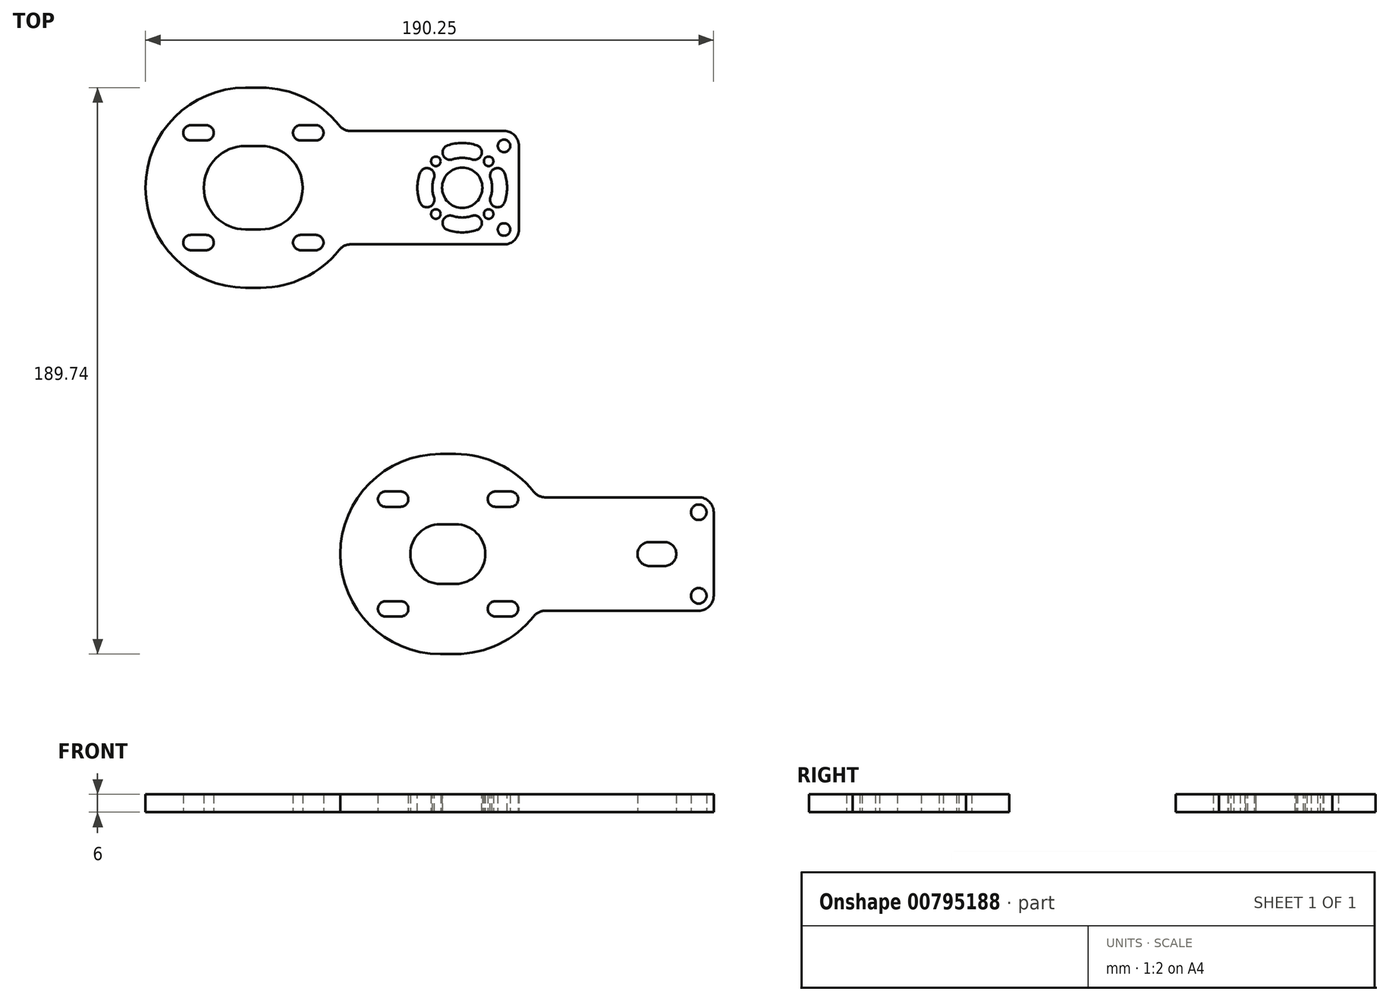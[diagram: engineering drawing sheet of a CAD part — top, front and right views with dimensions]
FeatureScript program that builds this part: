
annotation { "Feature Type Name" : "Feature", "Feature Type Description" : "" }
export const myFeature = defineFeature(function(context is Context, id is Id, definition is map)
    precondition{}
    {
        {
            var Q0;
            Q0=qCreatedBy(makeId("Top.planeOp"),FACE);
            var sketch = newSketch(context, id + "F0", { "sketchPlane" : qUnion([Q0])});
            skLineSegment(sketch, "E0.left", {"start": v(0, 33.5) * mm, "end": v(-0.07, -16.5) * mm, "construction": true});
            skLineSegment(sketch, "E0.right", {"start": v(90, 33.37) * mm, "end": v(89.93, -16.63) * mm});
            skCircle(sketch, "E1", {"center": v(69.95, 0) * mm, "radius": 6.75 * mm, "construction": true});
            skLineSegment(sketch, "E2.bottom", {"start": v(45.4, -41.12) * mm, "end": v(-45.4, -41.12) * mm, "construction": true});
            skLineSegment(sketch, "E2.top", {"start": v(45.4, 41.12) * mm, "end": v(-45.4, 41.12) * mm, "construction": true});
            skLineSegment(sketch, "E2.right", {"start": v(-45.4, -41.12) * mm, "end": v(-45.4, 41.12) * mm, "construction": true});
            skPoint(sketch, "E2.middle", {"position": v(0, 0) * mm});
            skCircle(sketch, "E3", {"center": v(69.95, 0) * mm, "radius": 6.75 * mm});
            skLineSegment(sketch, "E4", {"start": v(69.95, 0) * mm, "end": v(61.11, 8.84) * mm, "construction": true});
            skCircle(sketch, "E5", {"center": v(61.11, 8.84) * mm, "radius": 1.6 * mm});
            skCircle(sketch, "E6.1.0", {"center": v(61.11, -8.84) * mm, "radius": 1.6 * mm});
            skCircle(sketch, "E6.2.0", {"center": v(78.8, -8.84) * mm, "radius": 1.6 * mm});
            skCircle(sketch, "E6.3.0", {"center": v(78.8, 8.84) * mm, "radius": 1.6 * mm});
            skLineSegment(sketch, "E7", {"start": v(61.11, 8.84) * mm, "end": v(66.11, 8.84) * mm});
            skLineSegment(sketch, "E8", {"start": v(61.11, -8.84) * mm, "end": v(66.11, -8.84) * mm});
            skLineSegment(sketch, "E9", {"start": v(78.8, -8.84) * mm, "end": v(83.8, -8.84) * mm});
            skLineSegment(sketch, "E10", {"start": v(78.8, 8.84) * mm, "end": v(83.8, 8.84) * mm});
            skLineSegment(sketch, "E11", {"start": v(69.95, 0) * mm, "end": v(74.95, 0) * mm});
            skArc(sketch, "E12.0.startCap", {"start": v(78.8, 7.24) * mm, "mid": v(77.2, 8.84) * mm, "end": v(78.8, 10.44) * mm});
            skArc(sketch, "E12.0.endCap", {"start": v(83.8, 10.44) * mm, "mid": v(85.4, 8.84) * mm, "end": v(83.8, 7.24) * mm});
            skArc(sketch, "E13.0.startCap", {"start": v(61.11, 7.24) * mm, "mid": v(59.51, 8.84) * mm, "end": v(61.11, 10.44) * mm});
            skArc(sketch, "E13.1.startCap", {"start": v(61.11, -10.44) * mm, "mid": v(59.51, -8.84) * mm, "end": v(61.11, -7.24) * mm});
            skArc(sketch, "E13.2.startCap", {"start": v(78.8, -10.44) * mm, "mid": v(77.2, -8.84) * mm, "end": v(78.8, -7.24) * mm});
            skArc(sketch, "E13.2.endCap", {"start": v(83.8, -7.24) * mm, "mid": v(85.4, -8.84) * mm, "end": v(83.8, -10.44) * mm});
            skArc(sketch, "E14.0.startCap", {"start": v(69.95, -6.75) * mm, "mid": v(63.2, 0) * mm, "end": v(69.95, 6.75) * mm});
            skArc(sketch, "E14.0.endCap", {"start": v(74.95, 6.75) * mm, "mid": v(81.7, 0) * mm, "end": v(74.95, -6.75) * mm});
            skArc(sketch, "E15", {"start": v(74.95, -19) * mm, "mid": v(93.95, 0) * mm, "end": v(74.95, 19) * mm, "construction": true});
            skLineSegment(sketch, "E16", {"start": v(74.95, 19) * mm, "end": v(32.6, 19) * mm});
            skLineSegment(sketch, "E17", {"start": v(74.95, -19) * mm, "end": v(32.6, -19) * mm});
            skPoint(sketch, "E18.visualSharp", {"position": v(27.6, 19) * mm});
            skCircle(sketch, "E19", {"center": v(0, 0) * mm, "radius": 26 * mm, "construction": true});
            skCircle(sketch, "E20", {"center": v(0, 0) * mm, "radius": 16 * mm, "construction": true});
            skLineSegment(sketch, "E21", {"start": v(0, 0) * mm, "end": v(-28.53, 28.53) * mm, "construction": true});
            skCircle(sketch, "E22", {"center": v(-18.38, 18.38) * mm, "radius": 2.55 * mm, "construction": true});
            skCircle(sketch, "E23.1.0", {"center": v(-18.38, -18.38) * mm, "radius": 2.55 * mm, "construction": true});
            skCircle(sketch, "E23.2.0", {"center": v(18.38, -18.38) * mm, "radius": 2.55 * mm, "construction": true});
            skCircle(sketch, "E23.3.0", {"center": v(18.38, 18.38) * mm, "radius": 2.55 * mm, "construction": true});
            skLineSegment(sketch, "E24", {"start": v(15.83, 18.38) * mm, "end": v(20.93, 18.38) * mm});
            skLineSegment(sketch, "E25", {"start": v(15.83, -18.38) * mm, "end": v(20.93, -18.38) * mm});
            skLineSegment(sketch, "E26", {"start": v(-20.93, -18.38) * mm, "end": v(-15.83, -18.38) * mm});
            skLineSegment(sketch, "E27", {"start": v(-20.93, 18.38) * mm, "end": v(-15.83, 18.38) * mm});
            skArc(sketch, "E28.0.startCap", {"start": v(-20.93, 15.83) * mm, "mid": v(-23.48, 18.38) * mm, "end": v(-20.93, 20.93) * mm});
            skArc(sketch, "E28.0.endCap", {"start": v(-15.83, 20.93) * mm, "mid": v(-13.28, 18.38) * mm, "end": v(-15.83, 15.83) * mm});
            skLineSegment(sketch, "E28.0.left", {"start": v(-20.93, 20.93) * mm, "end": v(-15.83, 20.93) * mm});
            skLineSegment(sketch, "E28.0.right", {"start": v(-20.93, 15.83) * mm, "end": v(-15.83, 15.83) * mm});
            skArc(sketch, "E29.0.startCap", {"start": v(15.83, 15.83) * mm, "mid": v(13.28, 18.38) * mm, "end": v(15.83, 20.93) * mm});
            skArc(sketch, "E29.0.endCap", {"start": v(20.93, 20.93) * mm, "mid": v(23.48, 18.38) * mm, "end": v(20.93, 15.83) * mm});
            skLineSegment(sketch, "E29.0.left", {"start": v(15.83, 20.93) * mm, "end": v(20.93, 20.93) * mm});
            skLineSegment(sketch, "E29.0.right", {"start": v(15.83, 15.83) * mm, "end": v(20.93, 15.83) * mm});
            skArc(sketch, "E30.0.startCap", {"start": v(15.83, -20.93) * mm, "mid": v(13.28, -18.38) * mm, "end": v(15.83, -15.83) * mm});
            skArc(sketch, "E30.0.endCap", {"start": v(20.93, -15.83) * mm, "mid": v(23.48, -18.38) * mm, "end": v(20.93, -20.93) * mm});
            skLineSegment(sketch, "E30.0.left", {"start": v(15.83, -15.83) * mm, "end": v(20.93, -15.83) * mm});
            skLineSegment(sketch, "E30.0.right", {"start": v(15.83, -20.93) * mm, "end": v(20.93, -20.93) * mm});
            skArc(sketch, "E31.0.startCap", {"start": v(-20.93, -20.93) * mm, "mid": v(-23.48, -18.38) * mm, "end": v(-20.93, -15.83) * mm});
            skArc(sketch, "E31.0.endCap", {"start": v(-15.83, -15.83) * mm, "mid": v(-13.28, -18.38) * mm, "end": v(-15.83, -20.93) * mm});
            skLineSegment(sketch, "E31.0.left", {"start": v(-20.93, -15.83) * mm, "end": v(-15.83, -15.83) * mm});
            skLineSegment(sketch, "E31.0.right", {"start": v(-20.93, -20.93) * mm, "end": v(-15.83, -20.93) * mm});
            skLineSegment(sketch, "E32", {"start": v(2.5, 0) * mm, "end": v(-2.6, 0) * mm});
            skArc(sketch, "E33.0.startCap", {"start": v(2.5, 14) * mm, "mid": v(16.5, 0) * mm, "end": v(2.5, -14) * mm});
            skArc(sketch, "E33.0.endCap", {"start": v(-2.6, -14) * mm, "mid": v(-16.6, 0) * mm, "end": v(-2.6, 14) * mm});
            skLineSegment(sketch, "E33.0.left", {"start": v(2.5, -14) * mm, "end": v(-2.6, -14) * mm});
            skLineSegment(sketch, "E33.0.right", {"start": v(2.5, 14) * mm, "end": v(-2.6, 14) * mm});
            skArc(sketch, "E34.0.startCap", {"start": v(2.5, 33.5) * mm, "mid": v(17.04, 30.18) * mm, "end": v(28.7, 20.88) * mm});
            skArc(sketch, "E34.0.endCap", {"start": v(-2.6, -33.5) * mm, "mid": v(-36.1, 0) * mm, "end": v(-2.6, 33.5) * mm});
            skLineSegment(sketch, "E34.0.left", {"start": v(2.5, -33.5) * mm, "end": v(-2.6, -33.5) * mm});
            skLineSegment(sketch, "E34.0.right", {"start": v(2.5, 33.5) * mm, "end": v(-2.6, 33.5) * mm});
            skArc(sketch, "E35.trimOffspring", {"start": v(28.7, -20.88) * mm, "mid": v(17.04, -30.18) * mm, "end": v(2.5, -33.5) * mm});
            skPoint(sketch, "E36.visualSharp", {"position": v(30.1, 19) * mm});
            skArc(sketch, "E36.filletArc", {"start": v(28.7, 20.88) * mm, "mid": v(30.44, 19.5) * mm, "end": v(32.6, 19) * mm});
            skPoint(sketch, "E37.visualSharp", {"position": v(30.1, -19) * mm});
            skArc(sketch, "E37.filletArc", {"start": v(32.6, -19) * mm, "mid": v(30.44, -19.5) * mm, "end": v(28.7, -20.88) * mm});
            skLineSegment(sketch, "E38.bottom", {"start": v(83.95, 19) * mm, "end": v(50.95, 19) * mm});
            skLineSegment(sketch, "E38.top", {"start": v(83.95, -19) * mm, "end": v(50.95, -19) * mm});
            skLineSegment(sketch, "E38.left", {"start": v(88.95, 14) * mm, "end": v(88.95, -14) * mm});
            skLineSegment(sketch, "E38.right", {"start": v(50.95, 19) * mm, "end": v(50.95, -19) * mm});
            skPoint(sketch, "E39.visualSharp", {"position": v(88.95, 19) * mm});
            skArc(sketch, "E39.filletArc", {"start": v(88.95, 14) * mm, "mid": v(87.49, 17.54) * mm, "end": v(83.95, 19) * mm});
            skPoint(sketch, "E40.visualSharp", {"position": v(88.95, -19) * mm});
            skArc(sketch, "E40.filletArc", {"start": v(83.95, -19) * mm, "mid": v(87.49, -17.54) * mm, "end": v(88.95, -14) * mm});
            skCircle(sketch, "E41", {"center": v(83.95, 14) * mm, "radius": 2.1 * mm});
            skCircle(sketch, "E42", {"center": v(83.95, -14) * mm, "radius": 2.1 * mm});
            skSolve(sketch);
        }
        {
            var Q0;
            Q0=qSketchRegion(id+"F0",true);
            extrude(context, id + "F1", {"entities" : qUnion([Q0]), "depth" : 6 * mm, "offsetDistance" : 25 * mm});
        }
        {
            var Q0;
            Q0=makeQuery(id+"F1.opExtrude","CAP_FACE",FACE,{"disambiguationData":[OSD([sQuery(id+"F0.wireOp",EDGE,"H2Rf1mUt-0jlt-27wB-YffO-BGlGPGkjmCcf"),sQuery(id+"F0.wireOp",EDGE,"pAdha1hi-vLvk-yrs3-a5r3-yK9QRZCf7Ppp"),sQuery(id+"F0.wireOp",EDGE,"qyuHHp5k-pOz1-b6pl-9DLs-GjlQiXBvs5dg"),sQuery(id+"F0.wireOp",EDGE,"E3"),sQuery(id+"F0.wireOp",EDGE,"E5"),sQuery(id+"F0.wireOp",EDGE,"E6.1.0"),sQuery(id+"F0.wireOp",EDGE,"E6.2.0"),sQuery(id+"F0.wireOp",EDGE,"E6.3.0"),sQuery(id+"F0.wireOp",EDGE,"E16"),sQuery(id+"F0.wireOp",EDGE,"E17"),sQuery(id+"F0.wireOp",EDGE,"E18.filletArc"),sQuery(id+"F0.wireOp",EDGE,"bb5d5ffc-c1ad-4c8e-af76-ad25ce88a9b4.filletArc"),sQuery(id+"F0.wireOp",EDGE,"E22"),sQuery(id+"F0.wireOp",EDGE,"E23.1.0"),sQuery(id+"F0.wireOp",EDGE,"E23.2.0"),sQuery(id+"F0.wireOp",EDGE,"E23.3.0")])],"isStart":false});
            var sketch = newSketch(context, id + "F2", { "sketchPlane" : qUnion([Q0])});
            skArc(sketch, "E43", {"start": v(58.13, 4.07) * mm, "mid": v(57.45, 0) * mm, "end": v(58.13, -4.07) * mm});
            skLineSegment(sketch, "E44", {"start": v(69.95, 0) * mm, "end": v(55.62, 4.93) * mm, "construction": true});
            skLineSegment(sketch, "E45", {"start": v(69.95, 0) * mm, "end": v(55.25, -5.06) * mm, "construction": true});
            skArc(sketch, "E46.0.startCap", {"start": v(55.77, 4.88) * mm, "mid": v(58.95, 6.43) * mm, "end": v(60.5, 3.26) * mm});
            skArc(sketch, "E46.0.endCap", {"start": v(60.5, -3.26) * mm, "mid": v(58.95, -6.43) * mm, "end": v(55.77, -4.88) * mm});
            skArc(sketch, "E46.0.left", {"start": v(60.5, 3.26) * mm, "mid": v(59.95, 0) * mm, "end": v(60.5, -3.26) * mm});
            skArc(sketch, "E46.0.right", {"start": v(55.77, 4.88) * mm, "mid": v(54.95, 0) * mm, "end": v(55.77, -4.88) * mm});
            skArc(sketch, "E47.1.0", {"start": v(65.07, -14.18) * mm, "mid": v(63.52, -11) * mm, "end": v(66.7, -9.46) * mm});
            skArc(sketch, "E47.1.1", {"start": v(66.7, -9.46) * mm, "mid": v(69.95, -10) * mm, "end": v(73.2, -9.46) * mm});
            skArc(sketch, "E47.1.2", {"start": v(73.2, -9.46) * mm, "mid": v(76.39, -11) * mm, "end": v(74.84, -14.18) * mm});
            skArc(sketch, "E47.1.3", {"start": v(65.07, -14.18) * mm, "mid": v(69.95, -15) * mm, "end": v(74.84, -14.18) * mm});
            skArc(sketch, "E47.2.0", {"start": v(84.14, -4.88) * mm, "mid": v(80.96, -6.43) * mm, "end": v(79.4, -3.26) * mm});
            skArc(sketch, "E47.2.1", {"start": v(79.4, -3.26) * mm, "mid": v(79.95, 0) * mm, "end": v(79.4, 3.26) * mm});
            skArc(sketch, "E47.2.2", {"start": v(79.4, 3.26) * mm, "mid": v(80.96, 6.43) * mm, "end": v(84.14, 4.88) * mm});
            skArc(sketch, "E47.2.3", {"start": v(84.14, -4.88) * mm, "mid": v(84.95, 0) * mm, "end": v(84.14, 4.88) * mm});
            skArc(sketch, "E47.3.0", {"start": v(74.84, 14.18) * mm, "mid": v(76.39, 11) * mm, "end": v(73.2, 9.46) * mm});
            skArc(sketch, "E47.3.1", {"start": v(73.2, 9.46) * mm, "mid": v(69.95, 10) * mm, "end": v(66.7, 9.46) * mm});
            skArc(sketch, "E47.3.2", {"start": v(66.7, 9.46) * mm, "mid": v(63.52, 11) * mm, "end": v(65.07, 14.18) * mm});
            skArc(sketch, "E47.3.3", {"start": v(74.84, 14.18) * mm, "mid": v(69.95, 15) * mm, "end": v(65.07, 14.18) * mm});
            skSolve(sketch);
        }
        {
            var Q0;
            Q0=qSketchRegion(id+"F2",true);
            extrude(context, id + "F3", {"entities" : qUnion([Q0]), "operationType" : NewBodyOperationType.REMOVE, "oppositeDirection" : true, "depth" : 25 * mm, "offsetDistance" : 25 * mm});
        }
        {
            var Q0;
            Q0=qCreatedBy(makeId("Top.planeOp"),FACE);
            var sketch = newSketch(context, id + "F4", { "sketchPlane" : qUnion([Q0])});
            skLineSegment(sketch, "E48.left", {"start": v(65.2, -89.24) * mm, "end": v(65.13, -139.24) * mm, "construction": true});
            skPoint(sketch, "E49.middle", {"position": v(65.2, -122.74) * mm});
            skArc(sketch, "E50", {"start": v(140.15, -141.74) * mm, "mid": v(159.15, -122.74) * mm, "end": v(140.15, -103.74) * mm, "construction": true});
            skLineSegment(sketch, "E51", {"start": v(140.15, -103.74) * mm, "end": v(97.8, -103.74) * mm});
            skLineSegment(sketch, "E52", {"start": v(140.15, -141.74) * mm, "end": v(97.8, -141.74) * mm});
            skPoint(sketch, "E53.visualSharp", {"position": v(92.79, -103.74) * mm});
            skCircle(sketch, "E54", {"center": v(65.2, -122.74) * mm, "radius": 26 * mm, "construction": true});
            skCircle(sketch, "E55", {"center": v(65.2, -122.74) * mm, "radius": 16 * mm, "construction": true});
            skLineSegment(sketch, "E56", {"start": v(65.2, -122.74) * mm, "end": v(36.67, -94.2) * mm, "construction": true});
            skCircle(sketch, "E57", {"center": v(46.81, -104.35) * mm, "radius": 2.55 * mm, "construction": true});
            skCircle(sketch, "E58.1.0", {"center": v(46.81, -141.12) * mm, "radius": 2.55 * mm, "construction": true});
            skCircle(sketch, "E58.2.0", {"center": v(83.58, -141.12) * mm, "radius": 2.55 * mm, "construction": true});
            skCircle(sketch, "E58.3.0", {"center": v(83.58, -104.35) * mm, "radius": 2.55 * mm, "construction": true});
            skLineSegment(sketch, "E59", {"start": v(81.03, -104.35) * mm, "end": v(86.13, -104.35) * mm});
            skLineSegment(sketch, "E60", {"start": v(81.03, -141.12) * mm, "end": v(86.13, -141.12) * mm});
            skLineSegment(sketch, "E61", {"start": v(44.26, -141.12) * mm, "end": v(49.36, -141.12) * mm});
            skLineSegment(sketch, "E62", {"start": v(44.26, -104.35) * mm, "end": v(49.36, -104.35) * mm});
            skArc(sketch, "E63.0.startCap", {"start": v(44.26, -106.9) * mm, "mid": v(41.71, -104.35) * mm, "end": v(44.26, -101.8) * mm});
            skArc(sketch, "E63.0.endCap", {"start": v(49.36, -101.8) * mm, "mid": v(51.91, -104.35) * mm, "end": v(49.36, -106.9) * mm});
            skLineSegment(sketch, "E63.0.left", {"start": v(44.26, -101.8) * mm, "end": v(49.36, -101.8) * mm});
            skLineSegment(sketch, "E63.0.right", {"start": v(44.26, -106.9) * mm, "end": v(49.36, -106.9) * mm});
            skArc(sketch, "E64.0.startCap", {"start": v(81.03, -106.9) * mm, "mid": v(78.48, -104.35) * mm, "end": v(81.03, -101.8) * mm});
            skArc(sketch, "E64.0.endCap", {"start": v(86.13, -101.8) * mm, "mid": v(88.68, -104.35) * mm, "end": v(86.13, -106.9) * mm});
            skLineSegment(sketch, "E64.0.left", {"start": v(81.03, -101.8) * mm, "end": v(86.13, -101.8) * mm});
            skLineSegment(sketch, "E64.0.right", {"start": v(81.03, -106.9) * mm, "end": v(86.13, -106.9) * mm});
            skArc(sketch, "E65.0.startCap", {"start": v(81.03, -143.67) * mm, "mid": v(78.48, -141.12) * mm, "end": v(81.03, -138.57) * mm});
            skArc(sketch, "E65.0.endCap", {"start": v(86.13, -138.57) * mm, "mid": v(88.68, -141.12) * mm, "end": v(86.13, -143.67) * mm});
            skLineSegment(sketch, "E65.0.left", {"start": v(81.03, -138.57) * mm, "end": v(86.13, -138.57) * mm});
            skLineSegment(sketch, "E65.0.right", {"start": v(81.03, -143.67) * mm, "end": v(86.13, -143.67) * mm});
            skArc(sketch, "E66.0.startCap", {"start": v(44.26, -143.67) * mm, "mid": v(41.71, -141.12) * mm, "end": v(44.26, -138.57) * mm});
            skArc(sketch, "E66.0.endCap", {"start": v(49.36, -138.57) * mm, "mid": v(51.91, -141.12) * mm, "end": v(49.36, -143.67) * mm});
            skLineSegment(sketch, "E66.0.left", {"start": v(44.26, -138.57) * mm, "end": v(49.36, -138.57) * mm});
            skLineSegment(sketch, "E66.0.right", {"start": v(44.26, -143.67) * mm, "end": v(49.36, -143.67) * mm});
            skLineSegment(sketch, "E67", {"start": v(67.7, -122.74) * mm, "end": v(62.6, -122.74) * mm});
            skArc(sketch, "E68.0.startCap", {"start": v(67.7, -112.74) * mm, "mid": v(77.7, -122.74) * mm, "end": v(67.7, -132.74) * mm});
            skArc(sketch, "E68.0.endCap", {"start": v(62.6, -132.74) * mm, "mid": v(52.6, -122.74) * mm, "end": v(62.6, -112.74) * mm});
            skLineSegment(sketch, "E68.0.left", {"start": v(67.7, -132.74) * mm, "end": v(62.6, -132.74) * mm});
            skLineSegment(sketch, "E68.0.right", {"start": v(67.7, -112.74) * mm, "end": v(62.6, -112.74) * mm});
            skArc(sketch, "E69.0.startCap", {"start": v(67.7, -89.24) * mm, "mid": v(82.24, -92.56) * mm, "end": v(93.9, -101.85) * mm});
            skArc(sketch, "E69.0.endCap", {"start": v(62.6, -156.24) * mm, "mid": v(29.1, -122.74) * mm, "end": v(62.6, -89.24) * mm});
            skLineSegment(sketch, "E69.0.left", {"start": v(67.7, -156.24) * mm, "end": v(62.6, -156.24) * mm});
            skLineSegment(sketch, "E69.0.right", {"start": v(67.7, -89.24) * mm, "end": v(62.6, -89.24) * mm});
            skArc(sketch, "E70.trimOffspring", {"start": v(93.9, -143.62) * mm, "mid": v(82.24, -152.92) * mm, "end": v(67.7, -156.24) * mm});
            skPoint(sketch, "E71.visualSharp", {"position": v(95.3, -103.74) * mm});
            skArc(sketch, "E71.filletArc", {"start": v(93.9, -101.85) * mm, "mid": v(95.64, -103.24) * mm, "end": v(97.8, -103.74) * mm});
            skPoint(sketch, "E72.visualSharp", {"position": v(95.3, -141.74) * mm});
            skArc(sketch, "E72.filletArc", {"start": v(97.8, -141.74) * mm, "mid": v(95.64, -142.23) * mm, "end": v(93.9, -143.62) * mm});
            skLineSegment(sketch, "E73.bottom", {"start": v(149.15, -103.74) * mm, "end": v(116.15, -103.74) * mm});
            skLineSegment(sketch, "E73.top", {"start": v(149.15, -141.74) * mm, "end": v(116.15, -141.74) * mm});
            skLineSegment(sketch, "E73.left", {"start": v(154.15, -108.74) * mm, "end": v(154.15, -136.74) * mm});
            skPoint(sketch, "E74.visualSharp", {"position": v(154.15, -103.74) * mm});
            skArc(sketch, "E74.filletArc", {"start": v(154.15, -108.74) * mm, "mid": v(152.69, -105.2) * mm, "end": v(149.15, -103.74) * mm});
            skPoint(sketch, "E75.visualSharp", {"position": v(154.15, -141.74) * mm});
            skArc(sketch, "E75.filletArc", {"start": v(149.15, -141.74) * mm, "mid": v(152.69, -140.27) * mm, "end": v(154.15, -136.74) * mm});
            skLineSegment(sketch, "E76", {"start": v(135.15, -122.74) * mm, "end": v(126.31, -113.9) * mm, "construction": true});
            skPoint(sketch, "E77.center", {"position": v(135.15, -122.74) * mm});
            skLineSegment(sketch, "E78", {"start": v(126.31, -113.9) * mm, "end": v(131.31, -113.9) * mm});
            skLineSegment(sketch, "E79", {"start": v(126.31, -131.58) * mm, "end": v(131.31, -131.58) * mm});
            skLineSegment(sketch, "E80", {"start": v(144, -131.58) * mm, "end": v(149, -131.58) * mm});
            skLineSegment(sketch, "E81", {"start": v(144, -113.9) * mm, "end": v(149, -113.9) * mm});
            skArc(sketch, "E82.0.startCap", {"start": v(144, -115.5) * mm, "mid": v(142.4, -113.9) * mm, "end": v(144, -112.3) * mm});
            skArc(sketch, "E82.0.endCap", {"start": v(149, -112.3) * mm, "mid": v(150.6, -113.9) * mm, "end": v(149, -115.5) * mm});
            skArc(sketch, "E83.0.startCap", {"start": v(126.31, -115.5) * mm, "mid": v(124.71, -113.9) * mm, "end": v(126.31, -112.3) * mm});
            skArc(sketch, "E83.1.startCap", {"start": v(126.31, -133.18) * mm, "mid": v(124.71, -131.58) * mm, "end": v(126.31, -129.98) * mm});
            skArc(sketch, "E83.2.startCap", {"start": v(144, -133.18) * mm, "mid": v(142.4, -131.58) * mm, "end": v(144, -129.98) * mm});
            skArc(sketch, "E83.2.endCap", {"start": v(149, -129.98) * mm, "mid": v(150.6, -131.58) * mm, "end": v(149, -133.18) * mm});
            skArc(sketch, "E84.0.startCap", {"start": v(135.15, -129.49) * mm, "mid": v(128.4, -122.74) * mm, "end": v(135.15, -115.99) * mm});
            skCircle(sketch, "E85", {"center": v(149.15, -108.74) * mm, "radius": 2.6 * mm});
            skCircle(sketch, "E86", {"center": v(149.15, -136.74) * mm, "radius": 2.6 * mm});
            skLineSegment(sketch, "E87", {"start": v(132.65, -122.74) * mm, "end": v(137.65, -122.74) * mm});
            skArc(sketch, "E88.0.startCap", {"start": v(132.65, -126.74) * mm, "mid": v(128.65, -122.74) * mm, "end": v(132.65, -118.74) * mm});
            skArc(sketch, "E88.0.endCap", {"start": v(137.65, -118.74) * mm, "mid": v(141.65, -122.74) * mm, "end": v(137.65, -126.74) * mm});
            skLineSegment(sketch, "E88.0.left", {"start": v(132.65, -118.74) * mm, "end": v(137.65, -118.74) * mm});
            skLineSegment(sketch, "E88.0.right", {"start": v(132.65, -126.74) * mm, "end": v(137.65, -126.74) * mm});
            skSolve(sketch);
        }
        {
            var Q0;
            Q0 = qSketchRegion(id + "F4", true);
            extrude(context, id + "F5", {"entities" : qUnion([Q0]), "depth" : 6 * mm, "offsetDistance" : 25 * mm});
        }
    });
